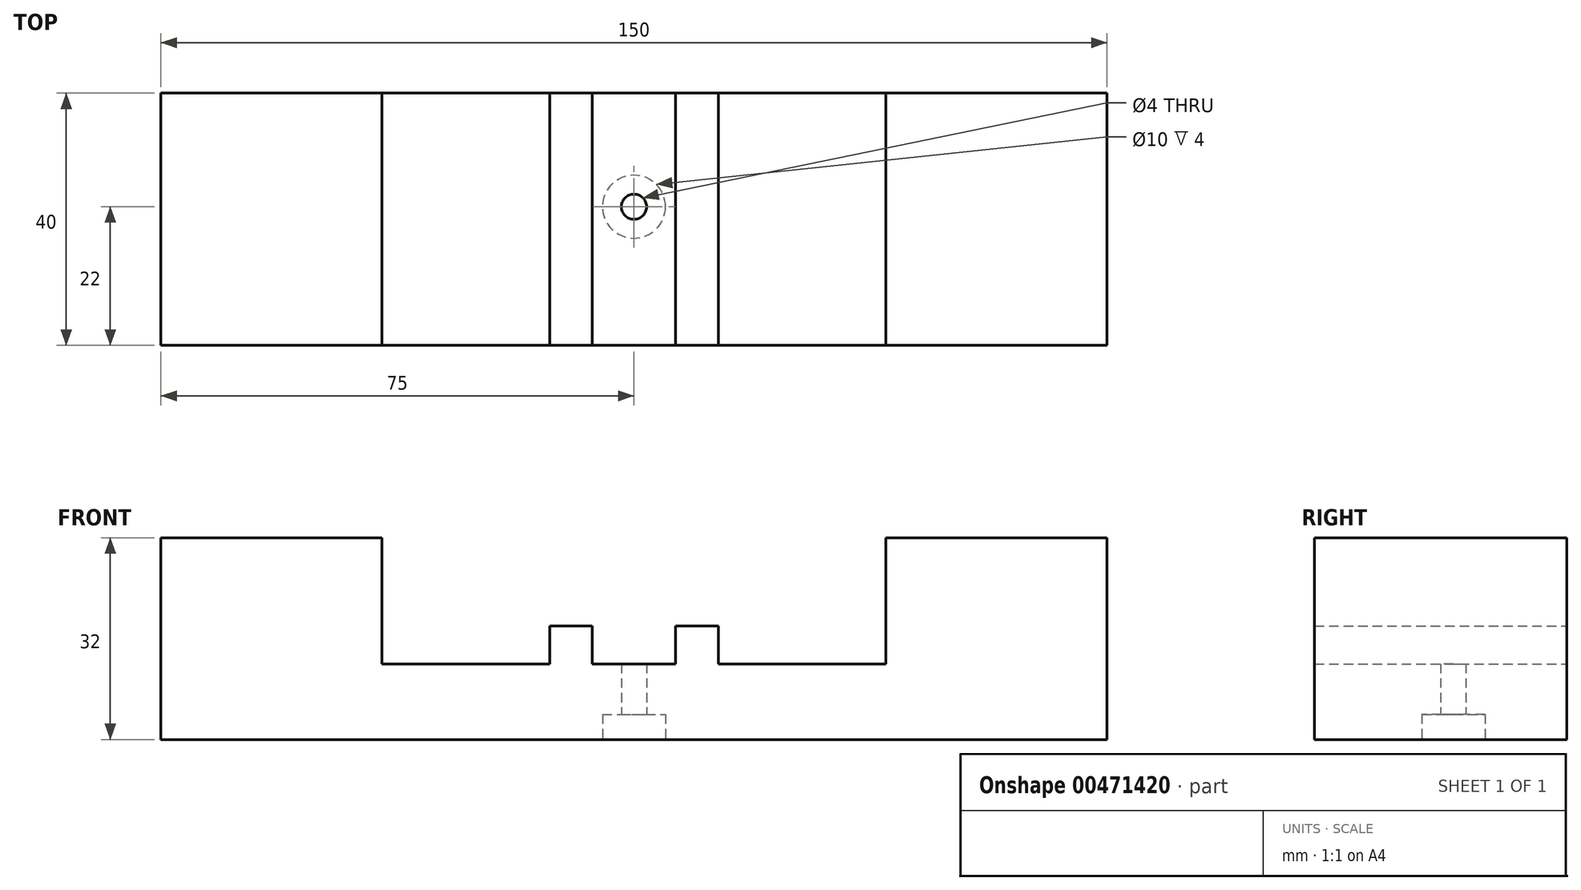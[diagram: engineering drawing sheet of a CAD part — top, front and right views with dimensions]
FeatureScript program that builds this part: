
annotation { "Feature Type Name" : "Feature", "Feature Type Description" : "" }
export const myFeature = defineFeature(function(context is Context, id is Id, definition is map)
    precondition{}
    {
        {
            var Q0;
            Q0=qCreatedBy(makeId("Front.planeOp"),FACE);
            var sketch = newSketch(context, id + "F0", { "sketchPlane" : qUnion([Q0])});
            skLineSegment(sketch, "E0.bottom", {"start": v(-75, 16) * mm, "end": v(-39.95, 16) * mm});
            skLineSegment(sketch, "E0.top", {"start": v(-75, -16) * mm, "end": v(75, -16) * mm});
            skLineSegment(sketch, "E0.left", {"start": v(-75, 16) * mm, "end": v(-75, -16) * mm});
            skLineSegment(sketch, "E0.right", {"start": v(75, 16) * mm, "end": v(75, -16) * mm});
            skLineSegment(sketch, "E1.top", {"start": v(-39.95, -4) * mm, "end": v(39.95, -4) * mm});
            skLineSegment(sketch, "E1.left", {"start": v(-39.95, 16) * mm, "end": v(-39.95, -4) * mm});
            skLineSegment(sketch, "E1.right", {"start": v(39.95, 16) * mm, "end": v(39.95, -4) * mm});
            skLineSegment(sketch, "E2.bottom", {"start": v(-13.38, -4) * mm, "end": v(-6.61, -4) * mm});
            skLineSegment(sketch, "E2.top", {"start": v(-13.38, 2) * mm, "end": v(-6.61, 2) * mm});
            skLineSegment(sketch, "E2.left", {"start": v(-13.38, -4) * mm, "end": v(-13.38, 2) * mm});
            skLineSegment(sketch, "E2.right", {"start": v(-6.61, -4) * mm, "end": v(-6.61, 2) * mm});
            skLineSegment(sketch, "E3.bottom", {"start": v(6.62, -4) * mm, "end": v(13.37, -4) * mm});
            skLineSegment(sketch, "E3.top", {"start": v(6.62, 2.02) * mm, "end": v(13.37, 2.02) * mm});
            skLineSegment(sketch, "E3.left", {"start": v(6.62, -4) * mm, "end": v(6.62, 2.02) * mm});
            skLineSegment(sketch, "E3.right", {"start": v(13.37, -4) * mm, "end": v(13.37, 2.02) * mm});
            skLineSegment(sketch, "E4.trimOffspring", {"start": v(39.95, 16) * mm, "end": v(75, 16) * mm});
            skSolve(sketch);
        }
        {
            var Q0;
            Q0 = qSketchRegion(id + "F0", true);
            extrude(context, id + "F1", {"entities" : qUnion([Q0]), "depth" : 40 * mm});
        }
        {
            var Q0;
            Q0=makeQuery(id+"F1.opExtrude","SWEPT_FACE",FACE,{"disambiguationData":[OSD([sQuery(id+"F0.wireOp",EDGE,"E0.top")])]});
            var sketch = newSketch(context, id + "F2", { "sketchPlane" : qUnion([Q0])});
            skCircle(sketch, "E5", {"center": v(0, 18) * mm, "radius": 2 * mm});
            skSolve(sketch);
        }
        {
            var Q0;
            Q0=sQuery(id+"F2.wireOp",VERTEX,"E5.center");
            var Q1;
            Q1=makeQuery(id+"F1.opExtrude","SWEPT_BODY",BODY,{"disambiguationData":[OSD([sQuery(id+"F0.wireOp",EDGE,"E0.bottom"),sQuery(id+"F0.wireOp",EDGE,"E0.top"),sQuery(id+"F0.wireOp",EDGE,"E0.left"),sQuery(id+"F0.wireOp",EDGE,"E0.right"),sQuery(id+"F0.wireOp",EDGE,"E1.top"),sQuery(id+"F0.wireOp",EDGE,"E1.left"),sQuery(id+"F0.wireOp",EDGE,"E1.right"),sQuery(id+"F0.wireOp",EDGE,"E2.top"),sQuery(id+"F0.wireOp",EDGE,"E2.left"),sQuery(id+"F0.wireOp",EDGE,"E2.right"),sQuery(id+"F0.wireOp",EDGE,"E3.top"),sQuery(id+"F0.wireOp",EDGE,"E3.left"),sQuery(id+"F0.wireOp",EDGE,"E3.right"),sQuery(id+"F0.wireOp",EDGE,"E4.trimOffspring")])]});
            hole(context, id + "F3", {"style" : HoleStyle.C_BORE, "endStyle" : HoleEndStyle.BLIND, "holeDiameter" : 4 * mm, "cBoreDiameter" : 10 * mm, "cBoreDepth" : 4 * mm, "holeDepth" : 25 * mm, "isTappedThrough" : true, "tappedDepth" : 12 * mm, "tapClearance" : 3, "startFromSketch" : true, "locations" : qUnion([Q0]), "scope" : qUnion([Q1])});
        }
    });
